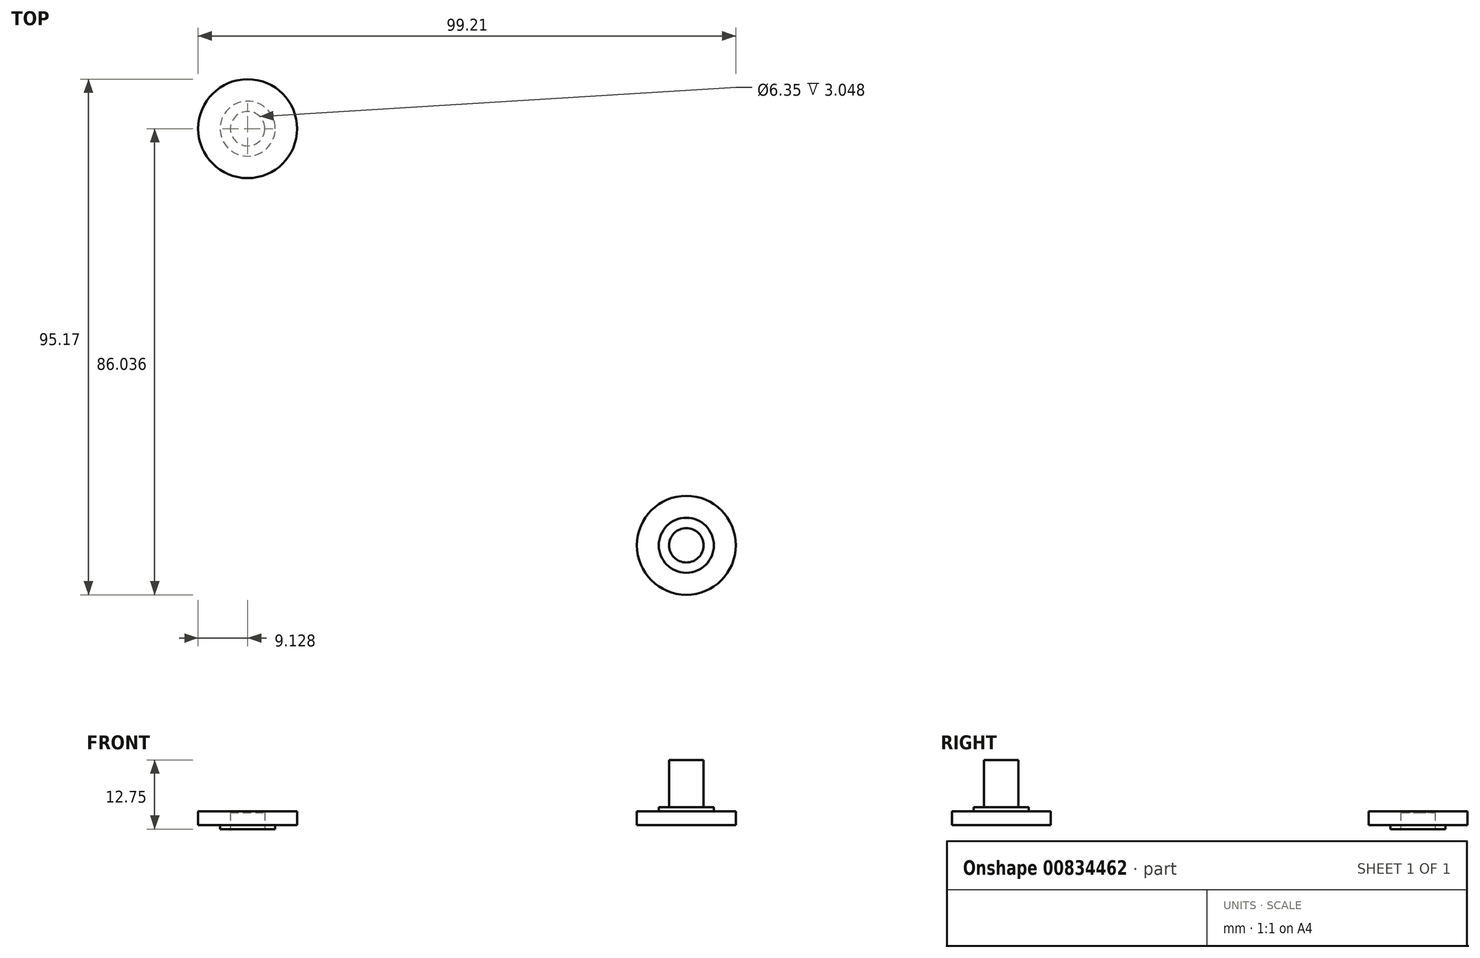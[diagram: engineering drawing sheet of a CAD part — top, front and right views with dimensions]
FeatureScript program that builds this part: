
annotation { "Feature Type Name" : "Feature", "Feature Type Description" : "" }
export const myFeature = defineFeature(function(context is Context, id is Id, definition is map)
    precondition{}
    {
        {
            var Q0;
            Q0=qCreatedBy(makeId("Top.planeOp"),FACE);
            var sketch = newSketch(context, id + "F0", { "sketchPlane" : qUnion([Q0])});
            skCircle(sketch, "E0", {"center": v(-41.42, 42.1) * mm, "radius": 9.13 * mm});
            skSolve(sketch);
        }
        {
            var Q0;
            Q0=makeQuery(id+"F0.imprint","IMPRINT",FACE,{"disambiguationData":[TD([[makeQuery(id+"F0.imprint","IMPRINT",EDGE,{"derivedFrom":sQuery(id+"F0.wireOp",EDGE,"E0")}),1.0]])]});
            extrude(context, id + "F1", {"entities" : qUnion([Q0]), "depth" : 2.54 * mm, "offsetDistance" : 25.4 * mm});
        }
        {
            var Q0;
            Q0=qCreatedBy(makeId("Top.planeOp"),FACE);
            var sketch = newSketch(context, id + "F2", { "sketchPlane" : qUnion([Q0])});
            skCircle(sketch, "E1", {"center": v(39.53, -34.81) * mm, "radius": 9.13 * mm});
            skSolve(sketch);
        }
        {
            var Q0;
            Q0=makeQuery(id+"F2.imprint","IMPRINT",FACE,{"disambiguationData":[TD([[makeQuery(id+"F2.imprint","IMPRINT",EDGE,{"derivedFrom":sQuery(id+"F2.wireOp",EDGE,"E1")}),1.0]])]});
            extrude(context, id + "F3", {"entities" : qUnion([Q0]), "depth" : 2.54 * mm, "offsetDistance" : 25.4 * mm});
        }
        {
            var Q0;
            Q0=makeQuery(id+"F3.opExtrude","CAP_FACE",FACE,{"disambiguationData":[OSD([sQuery(id+"F2.wireOp",EDGE,"E1")])],"isStart":false});
            var sketch = newSketch(context, id + "F4", { "sketchPlane" : qUnion([Q0])});
            skCircle(sketch, "E2", {"center": v(39.53, -34.81) * mm, "radius": 3.18 * mm});
            skSolve(sketch);
        }
        {
            var Q0;
            Q0=makeQuery(id+"F4.imprint","IMPRINT",FACE,{"disambiguationData":[TD([[makeQuery(id+"F4.imprint","IMPRINT",EDGE,{"derivedFrom":sQuery(id+"F4.wireOp",EDGE,"E2")}),1.0]])]});
            extrude(context, id + "F5", {"entities" : qUnion([Q0]), "operationType" : NewBodyOperationType.ADD, "depth" : 9.45 * mm, "offsetDistance" : 25.4 * mm});
        }
        {
            var Q0;
            Q0=makeQuery(id+"F1.opExtrude","CAP_FACE",FACE,{"disambiguationData":[OSD([sQuery(id+"F0.wireOp",EDGE,"E0")])],"isStart":true});
            var sketch = newSketch(context, id + "F6", { "sketchPlane" : qUnion([Q0])});
            skCircle(sketch, "E3", {"center": v(-41.42, -42.1) * mm, "radius": 3.18 * mm});
            skSolve(sketch);
        }
        {
            var Q0;
            Q0=makeQuery(id+"F6.imprint","IMPRINT",FACE,{"disambiguationData":[TD([[makeQuery(id+"F6.imprint","IMPRINT",EDGE,{"derivedFrom":sQuery(id+"F6.wireOp",EDGE,"E3")}),1.0]])]});
            extrude(context, id + "F7", {"entities" : qUnion([Q0]), "operationType" : NewBodyOperationType.ADD, "oppositeDirection" : true, "depth" : 1.78 * mm, "offsetDistance" : 25.4 * mm});
        }
        {
            var Q0;
            Q0=makeQuery(id+"F1.opExtrude","CAP_FACE",FACE,{"disambiguationData":[OSD([sQuery(id+"F0.wireOp",EDGE,"E0")])],"isStart":true});
            var sketch = newSketch(context, id + "F8", { "sketchPlane" : qUnion([Q0])});
            skCircle(sketch, "E4", {"center": v(-41.42, -42.1) * mm, "radius": 3.18 * mm});
            skSolve(sketch);
        }
        {
            var Q0;
            Q0=makeQuery(id+"F8.imprint","IMPRINT",FACE,{"disambiguationData":[TD([[makeQuery(id+"F8.imprint","IMPRINT",EDGE,{"derivedFrom":sQuery(id+"F8.wireOp",EDGE,"E4")}),1.0]])]});
            extrude(context, id + "F9", {"entities" : qUnion([Q0]), "operationType" : NewBodyOperationType.ADD, "oppositeDirection" : true, "depth" : 2.03 * mm, "offsetDistance" : 25.4 * mm});
        }
        {
            var Q0;
            Q0=makeQuery(id+"F1.opExtrude","CAP_FACE",FACE,{"disambiguationData":[OSD([sQuery(id+"F0.wireOp",EDGE,"E0")])],"isStart":true});
            var sketch = newSketch(context, id + "F10", { "sketchPlane" : qUnion([Q0])});
            skCircle(sketch, "E5", {"center": v(-41.42, -42.1) * mm, "radius": 3.18 * mm});
            skSolve(sketch);
        }
        {
            var Q0;
            Q0=makeQuery(id+"F10.imprint","IMPRINT",FACE,{"disambiguationData":[TD([[makeQuery(id+"F10.imprint","IMPRINT",EDGE,{"derivedFrom":sQuery(id+"F10.wireOp",EDGE,"E5")}),1.0]])]});
            extrude(context, id + "F11", {"entities" : qUnion([Q0]), "operationType" : NewBodyOperationType.REMOVE, "oppositeDirection" : true, "depth" : 2.3 * mm, "offsetDistance" : 25.4 * mm});
        }
        {
            var Q0;
            Q0=makeQuery(id+"F1.opExtrude","CAP_FACE",FACE,{"disambiguationData":[OSD([sQuery(id+"F0.wireOp",EDGE,"E0")])],"isStart":true});
            var sketch = newSketch(context, id + "F12", { "sketchPlane" : qUnion([Q0])});
            skCircle(sketch, "E6", {"center": v(-41.42, -42.1) * mm, "radius": 5.08 * mm});
            skSolve(sketch);
        }
        {
            var Q0;
            Q0=makeQuery(id+"F12.imprint","IMPRINT",FACE,{"disambiguationData":[TD([[makeQuery(id+"F12.imprint","IMPRINT",EDGE,{"derivedFrom":sQuery(id+"F12.wireOp",EDGE,"E6")}),1.0]])]});
            extrude(context, id + "F13", {"entities" : qUnion([Q0]), "operationType" : NewBodyOperationType.ADD, "depth" : 0.76 * mm, "offsetDistance" : 25.4 * mm});
        }
        {
            var Q0;
            Q0=makeQuery(id+"F3.opExtrude","CAP_FACE",FACE,{"disambiguationData":[OSD([sQuery(id+"F2.wireOp",EDGE,"E1")])],"isStart":false});
            var sketch = newSketch(context, id + "F14", { "sketchPlane" : qUnion([Q0])});
            skCircle(sketch, "E7", {"center": v(39.53, -34.81) * mm, "radius": 5.08 * mm});
            skSolve(sketch);
        }
        {
            var Q0;
            Q0=makeQuery(id+"F14.imprint","IMPRINT",FACE,{"disambiguationData":[TD([[makeQuery(id+"F14.imprint","IMPRINT",EDGE,{"derivedFrom":sQuery(id+"F14.wireOp",EDGE,"E7")}),1.0]])]});
            extrude(context, id + "F15", {"entities" : qUnion([Q0]), "operationType" : NewBodyOperationType.ADD, "depth" : 0.76 * mm, "offsetDistance" : 25.4 * mm});
        }
    });
